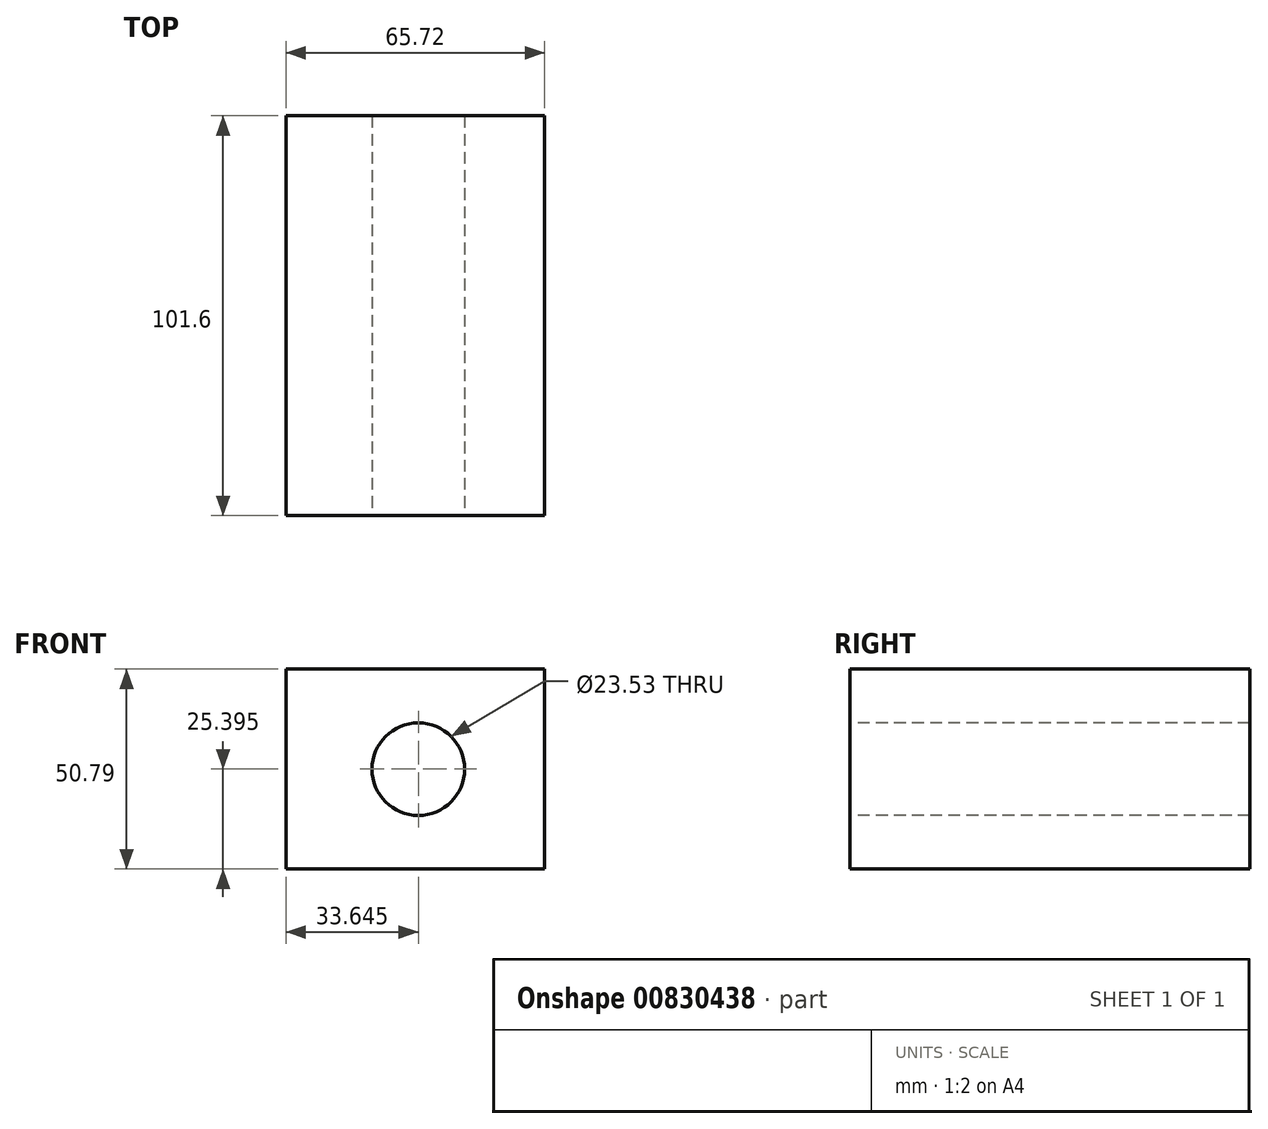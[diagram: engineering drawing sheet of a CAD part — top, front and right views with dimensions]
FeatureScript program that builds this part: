
annotation { "Feature Type Name" : "Feature", "Feature Type Description" : "" }
export const myFeature = defineFeature(function(context is Context, id is Id, definition is map)
    precondition{}
    {
        {
            var Q0;
            Q0=qCreatedBy(makeId("Front.planeOp"),FACE);
            var sketch = newSketch(context, id + "F0", { "sketchPlane" : qUnion([Q0])});
            skLineSegment(sketch, "E0.bottom", {"start": v(0, 0) * mm, "end": v(65.72, 0) * mm});
            skLineSegment(sketch, "E0.top", {"start": v(0, 50.79) * mm, "end": v(65.72, 50.79) * mm});
            skLineSegment(sketch, "E0.left", {"start": v(0, 0) * mm, "end": v(0, 50.79) * mm});
            skLineSegment(sketch, "E0.right", {"start": v(65.72, 0) * mm, "end": v(65.72, 50.79) * mm});
            skSolve(sketch);
        }
        {
            var Q0;
            Q0=makeQuery(id+"F0.imprint","IMPRINT",FACE,{"disambiguationData":[TD([[makeQuery(id+"F0.imprint","IMPRINT",EDGE,{"derivedFrom":sQuery(id+"F0.wireOp",EDGE,"E0.bottom")}),1.0]])]});
            extrude(context, id + "F1", {"entities" : qUnion([Q0]), "depth" : 101.6 * mm, "offsetDistance" : 25.4 * mm});
        }
        {
            var Q0;
            Q0=makeQuery(id+"F1.opExtrude","CAP_FACE",FACE,{"disambiguationData":[OSD([sQuery(id+"F0.wireOp",EDGE,"E0.bottom"),sQuery(id+"F0.wireOp",EDGE,"E0.top"),sQuery(id+"F0.wireOp",EDGE,"E0.left"),sQuery(id+"F0.wireOp",EDGE,"E0.right")])],"isStart":false});
            var sketch = newSketch(context, id + "F2", { "sketchPlane" : qUnion([Q0])});
            skCircle(sketch, "E1", {"center": v(33.64, 25.4) * mm, "radius": 11.77 * mm});
            skPoint(sketch, "E2", {"position": v(65.72, 25.4) * mm});
            skSolve(sketch);
        }
        {
            var Q0;
            Q0 = qSketchRegion(id + "F2", true);
            extrude(context, id + "F3", {"entities" : qUnion([Q0]), "operationType" : NewBodyOperationType.REMOVE, "oppositeDirection" : true, "depth" : 101.6 * mm, "offsetDistance" : 25.4 * mm});
        }
    });
